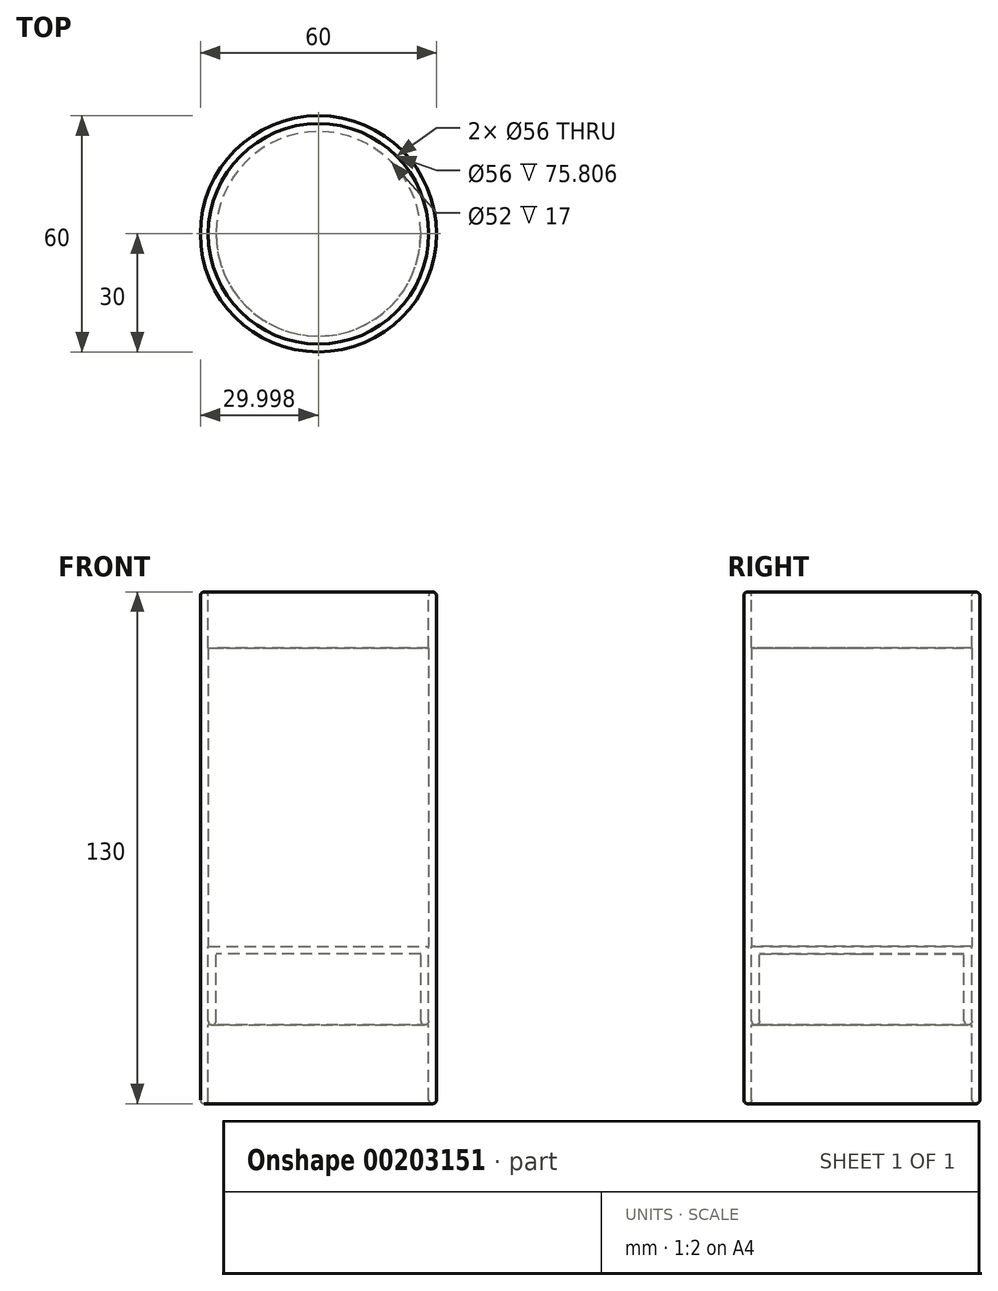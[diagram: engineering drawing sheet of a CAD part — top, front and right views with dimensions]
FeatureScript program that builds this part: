
annotation { "Feature Type Name" : "Feature", "Feature Type Description" : "" }
export const myFeature = defineFeature(function(context is Context, id is Id, definition is map)
    precondition{}
    {
        {
            var Q0;
            Q0=qCreatedBy(makeId("Front.planeOp"),FACE);
            var sketch = newSketch(context, id + "F0", { "sketchPlane" : qUnion([Q0])});
            skLineSegment(sketch, "E0", {"start": v(-23.66, 71.47) * mm, "end": v(-23.66, -58.53) * mm});
            skLineSegment(sketch, "E1", {"start": v(-23.66, 71.47) * mm, "end": v(-21.66, 71.47) * mm});
            skLineSegment(sketch, "E2", {"start": v(-21.66, 71.47) * mm, "end": v(-21.66, 57.27) * mm});
            skLineSegment(sketch, "E3", {"start": v(-23.66, -58.53) * mm, "end": v(-21.66, -58.53) * mm});
            skLineSegment(sketch, "E4", {"start": v(-21.66, -58.53) * mm, "end": v(-21.66, -38.53) * mm});
            skSolve(sketch);
        }
        {
            var Q0;
            Q0=qCreatedBy(makeId("Front.planeOp"),FACE);
            var sketch = newSketch(context, id + "F1", { "sketchPlane" : qUnion([Q0])});
            skLineSegment(sketch, "E5.0", {"start": v(-21.66, -58.53) * mm, "end": v(-21.66, -38.53) * mm});
            skLineSegment(sketch, "E6", {"start": v(-21.66, -38.53) * mm, "end": v(-21.66, -18.53) * mm});
            skLineSegment(sketch, "E7", {"start": v(-21.66, -38.53) * mm, "end": v(-19.66, -38.53) * mm});
            skLineSegment(sketch, "E8", {"start": v(-19.66, -38.53) * mm, "end": v(-19.66, -20.53) * mm});
            skLineSegment(sketch, "E9", {"start": v(-19.66, -20.53) * mm, "end": v(6.34, -20.53) * mm});
            skLineSegment(sketch, "E10", {"start": v(-21.66, -18.53) * mm, "end": v(6.34, -18.53) * mm});
            skSolve(sketch);
        }
        {
            var Q0;
            Q0=qCreatedBy(makeId("Front.planeOp"),FACE);
            var sketch = newSketch(context, id + "F2", { "sketchPlane" : qUnion([Q0])});
            skLineSegment(sketch, "E11", {"start": v(-21.66, -18.53) * mm, "end": v(6.34, -18.53) * mm});
            skLineSegment(sketch, "E12", {"start": v(-21.66, 57.27) * mm, "end": v(-21.66, -18.53) * mm});
            skPoint(sketch, "E13.0.start.orphan", {"position": v(-21.66, -38.53) * mm});
            skPoint(sketch, "E14.0.start.orphan", {"position": v(-21.66, 71.47) * mm});
            skLineSegment(sketch, "E15", {"start": v(6.34, -18.53) * mm, "end": v(6.34, 65.9) * mm, "construction": true});
            skSolve(sketch);
        }
        {
            var Q0;
            Q0=qCreatedBy(makeId("Front.planeOp"),FACE);
            var sketch = newSketch(context, id + "F3", { "sketchPlane" : qUnion([Q0])});
            skLineSegment(sketch, "E16", {"start": v(-21.66, 57.27) * mm, "end": v(6.34, 57.27) * mm});
            skPoint(sketch, "E17.0.end.orphan", {"position": v(-21.66, -18.53) * mm});
            skSolve(sketch);
        }
        {
            var Q0;
            Q0=sQuery(id+"F3.wireOp",EDGE,"E16");
            var Q1;
            Q1=sQuery(id+"F2.wireOp",EDGE,"E15");
            revolve(context, id + "F4", {"bodyType" : ToolBodyType.SURFACE, "surfaceEntities" : qUnion([Q0]), "axis" : qUnion([Q1]), "revolveType" : RevolveType.FULL});
        }
        {
            var Q0;
            Q0=qCreatedBy(makeId("Front.planeOp"),FACE);
            var sketch = newSketch(context, id + "F5", { "sketchPlane" : qUnion([Q0])});
            skLineSegment(sketch, "E18.0", {"start": v(-19.66, -20.53) * mm, "end": v(6.34, -20.53) * mm});
            skLineSegment(sketch, "E19", {"start": v(6.34, -20.53) * mm, "end": v(6.34, 51.2) * mm});
            skSolve(sketch);
        }
        {
            var Q0;
            Q0=sQuery(id+"F5.wireOp",EDGE,"E18.0");
            var Q1;
            Q1=sQuery(id+"F1.wireOp",EDGE,"E8");
            var Q2;
            Q2=sQuery(id+"F1.wireOp",EDGE,"E7");
            var Q3;
            Q3=sQuery(id+"F1.wireOp",EDGE,"E6");
            var Q4;
            Q4=sQuery(id+"F1.wireOp",EDGE,"E10");
            var Q5;
            Q5=sQuery(id+"F5.wireOp",EDGE,"E19");
            revolve(context, id + "F6", {"bodyType" : ToolBodyType.SURFACE, "surfaceEntities" : qUnion([Q0, Q1, Q2, Q3, Q4]), "axis" : qUnion([Q5]), "revolveType" : RevolveType.FULL});
        }
        {
            var Q0;
            Q0=qCreatedBy(makeId("Front.planeOp"),FACE);
            var sketch = newSketch(context, id + "F7", { "sketchPlane" : qUnion([Q0])});
            skLineSegment(sketch, "E20.0", {"start": v(34.34, 57.27) * mm, "end": v(-21.66, 57.27) * mm});
            skLineSegment(sketch, "E21", {"start": v(6.34, 57.27) * mm, "end": v(6.34, 36.22) * mm});
            skPoint(sketch, "E21.endSnap0", {"position": v(6.34, 57.27) * mm});
            skSolve(sketch);
        }
        {
            var Q0;
            Q0 = qSketchRegion(id + "F7", true);
            var Q1;
            Q1 = qSketchRegion(id + "F2", true);
            var Q2;
            Q2 = qConstructionFilter(qBodyType(qCreatedBy(id + "F2" ,EDGE), BodyType.WIRE), ConstructionObject.NO);
            var Q3;
            Q3=sQuery(id+"F7.wireOp",EDGE,"E21");
            revolve(context, id + "F8", {"bodyType" : ToolBodyType.SURFACE, "entities" : qUnion([Q0, Q1]), "surfaceEntities" : qUnion([Q2]), "axis" : qUnion([Q3]), "revolveType" : RevolveType.FULL});
        }
        {
            var Q0;
            Q0=qCreatedBy(makeId("Front.planeOp"),FACE);
            var sketch = newSketch(context, id + "F9", { "sketchPlane" : qUnion([Q0])});
            skLineSegment(sketch, "E22.0", {"start": v(-21.66, -38.53) * mm, "end": v(34.34, -38.53) * mm});
            skLineSegment(sketch, "E23", {"start": v(6.34, -38.53) * mm, "end": v(6.34, 48.1) * mm});
            skSolve(sketch);
        }
        {
            var Q0;
            Q0 = qConstructionFilter(qBodyType(qCreatedBy(id + "F0" ,EDGE), BodyType.WIRE), ConstructionObject.NO);
            var Q1;
            Q1=sQuery(id+"F9.wireOp",EDGE,"E23");
            revolve(context, id + "F10", {"bodyType" : ToolBodyType.SURFACE, "surfaceEntities" : qUnion([Q0]), "axis" : qUnion([Q1]), "revolveType" : RevolveType.FULL});
        }
        {
            var Q0;
            Q0=makeQuery(id+"F10.opRevolve","SWEPT_FACE",FACE,{"disambiguationData":[OSD([sQuery(id+"F0.wireOp",EDGE,"E1")])]});
            var Q1;
            Q1=makeQuery(id+"F10.opRevolve","SWEPT_FACE",FACE,{"disambiguationData":[OSD([sQuery(id+"F0.wireOp",EDGE,"E3")])]});
            var Q2;
            Q2=makeQuery(id+"F6.opRevolve","SWEPT_FACE",FACE,{"disambiguationData":[OSD([sQuery(id+"F1.wireOp",EDGE,"E7")])]});
            fillet(context, id + "F11", {"entities" : qUnion([Q0, Q1, Q2]), "radius" : 1 * mm, "tangentPropagation" : true, "allowEdgeOverflow" : false});
        }
    });
